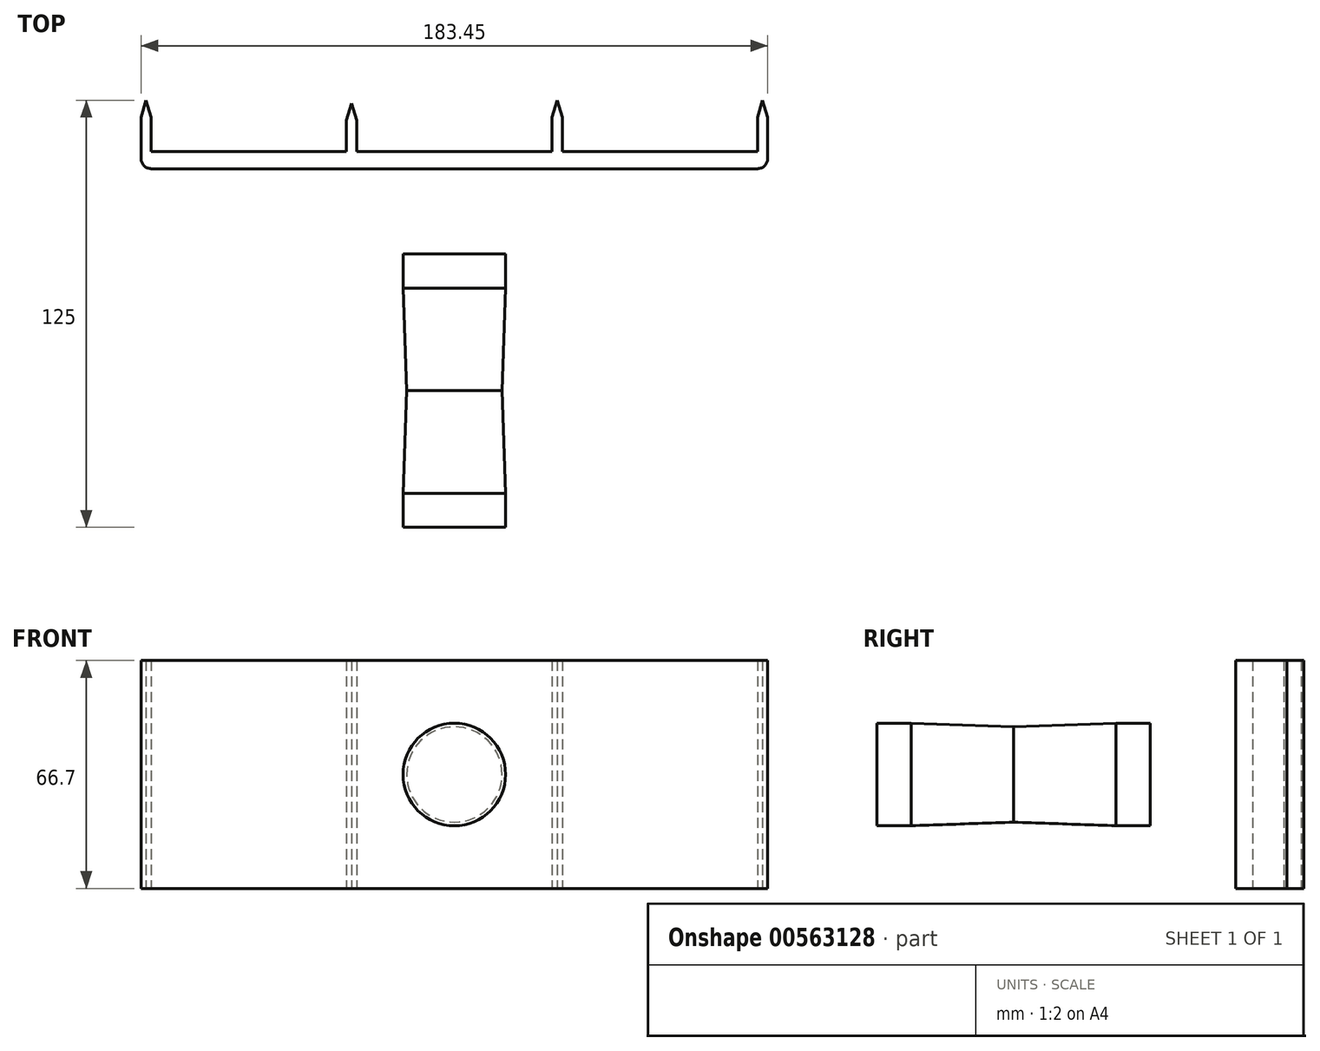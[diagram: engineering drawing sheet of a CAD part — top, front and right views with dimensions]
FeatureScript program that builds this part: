
annotation { "Feature Type Name" : "Feature", "Feature Type Description" : "" }
export const myFeature = defineFeature(function(context is Context, id is Id, definition is map)
    precondition{}
    {
        {
            var Q0;
            Q0=qCreatedBy(makeId("Top.planeOp"),FACE);
            var sketch = newSketch(context, id + "F0", { "sketchPlane" : qUnion([Q0])});
            skLineSegment(sketch, "E0", {"start": v(62.84, 0) * mm, "end": v(62.84, 10) * mm});
            skLineSegment(sketch, "E1", {"start": v(62.84, 0) * mm, "end": v(5.7, 0) * mm});
            skLineSegment(sketch, "E2", {"start": v(5.7, 0) * mm, "end": v(5.7, 10) * mm});
            skLineSegment(sketch, "E3.0", {"start": v(2.7, 0) * mm, "end": v(2.7, 10) * mm});
            skLineSegment(sketch, "E4", {"start": v(2.7, 0) * mm, "end": v(-54.46, 0) * mm});
            skLineSegment(sketch, "E5", {"start": v(-54.46, 0) * mm, "end": v(-54.46, 9.15) * mm});
            skLineSegment(sketch, "E6.0", {"start": v(-57.46, 0) * mm, "end": v(-57.46, 9.15) * mm});
            skLineSegment(sketch, "E7", {"start": v(-57.46, 0) * mm, "end": v(-114.6, 0) * mm});
            skLineSegment(sketch, "E8", {"start": v(-114.6, 0) * mm, "end": v(-114.6, 10) * mm});
            skLineSegment(sketch, "E9.0", {"start": v(-57.46, -5) * mm, "end": v(-114.6, -5) * mm});
            skLineSegment(sketch, "E10.0", {"start": v(2.7, -5) * mm, "end": v(-54.46, -5) * mm});
            skLineSegment(sketch, "E11.0", {"start": v(62.84, -5) * mm, "end": v(5.7, -5) * mm});
            skLineSegment(sketch, "E12", {"start": v(-57.46, -5) * mm, "end": v(-54.46, -5) * mm});
            skLineSegment(sketch, "E13", {"start": v(2.7, -5) * mm, "end": v(5.7, -5) * mm});
            skLineSegment(sketch, "E14.0", {"start": v(65.84, 0) * mm, "end": v(65.84, 10) * mm});
            skLineSegment(sketch, "E15.0", {"start": v(-117.6, 0) * mm, "end": v(-117.6, 10) * mm});
            skLineSegment(sketch, "E16", {"start": v(-117.6, 0) * mm, "end": v(-114.6, 0) * mm});
            skLineSegment(sketch, "E17", {"start": v(-117.6, 0) * mm, "end": v(-117.6, -2) * mm});
            skArc(sketch, "E18", {"start": v(-117.6, -2) * mm, "mid": v(-116.73, -4.12) * mm, "end": v(-114.6, -5) * mm});
            skLineSegment(sketch, "E19", {"start": v(65.84, 0) * mm, "end": v(62.84, 0) * mm});
            skLineSegment(sketch, "E20", {"start": v(65.84, 0) * mm, "end": v(65.84, -2) * mm});
            skArc(sketch, "E21", {"start": v(62.84, -5) * mm, "mid": v(64.96, -4.12) * mm, "end": v(65.84, -2) * mm});
            skLineSegment(sketch, "E22", {"start": v(-114.6, 10) * mm, "end": v(-117.6, 10) * mm});
            skLineSegment(sketch, "E23", {"start": v(-116.1, 10) * mm, "end": v(-116.1, 15) * mm});
            skPoint(sketch, "E23.endSnap0", {"position": v(-116.1, 10) * mm});
            skLineSegment(sketch, "E24", {"start": v(-116.1, 15) * mm, "end": v(-114.6, 10) * mm});
            skLineSegment(sketch, "E25", {"start": v(-116.1, 15) * mm, "end": v(-117.6, 10) * mm});
            skLineSegment(sketch, "E26", {"start": v(-57.46, 9.15) * mm, "end": v(-54.46, 9.15) * mm});
            skLineSegment(sketch, "E27", {"start": v(-55.96, 9.15) * mm, "end": v(-55.96, 14.15) * mm});
            skLineSegment(sketch, "E28", {"start": v(-55.96, 14.15) * mm, "end": v(-54.46, 9.15) * mm});
            skLineSegment(sketch, "E29", {"start": v(-55.96, 14.15) * mm, "end": v(-57.46, 9.15) * mm});
            skLineSegment(sketch, "E30", {"start": v(2.7, 10) * mm, "end": v(5.7, 10) * mm});
            skLineSegment(sketch, "E31", {"start": v(4.2, 10) * mm, "end": v(4.2, 15) * mm});
            skLineSegment(sketch, "E32", {"start": v(4.2, 15) * mm, "end": v(2.7, 10) * mm});
            skLineSegment(sketch, "E33", {"start": v(4.2, 15) * mm, "end": v(5.7, 10) * mm});
            skLineSegment(sketch, "E34", {"start": v(62.84, 10) * mm, "end": v(65.84, 10) * mm});
            skLineSegment(sketch, "E35", {"start": v(64.34, 10) * mm, "end": v(64.34, 15) * mm});
            skLineSegment(sketch, "E36", {"start": v(64.34, 15) * mm, "end": v(62.84, 10) * mm});
            skLineSegment(sketch, "E37", {"start": v(64.34, 15) * mm, "end": v(65.84, 10) * mm});
            skSolve(sketch);
        }
        {
            var Q0;
            Q0 = qSketchRegion(id + "F0", true);
            extrude(context, id + "F1", {"entities" : qUnion([Q0]), "endBound" : BoundingType.SYMMETRIC, "depth" : 66.7 * mm, "offsetDistance" : 25 * mm});
        }
        {
            var Q0;
            Q0=makeQuery(id+"F1.opExtrude","SWEPT_FACE",FACE,{"disambiguationData":[OSD([sQuery(id+"F0.wireOp",EDGE,"E9.0"),sQuery(id+"F0.wireOp",EDGE,"E10.0"),sQuery(id+"F0.wireOp",EDGE,"E11.0"),sQuery(id+"F0.wireOp",EDGE,"E12"),sQuery(id+"F0.wireOp",EDGE,"E13")])]});
            cPlane(context, id + "F2", {"entities" : qUnion([Q0]), "cplaneType" : CPlaneType.OFFSET, "offset" : 25 * mm, "width" : 150 * mm, "height" : 150 * mm});
        }
        {
            var Q0;
            Q0=qCreatedBy(id+"F2.planeOp",FACE);
            var sketch = newSketch(context, id + "F3", { "sketchPlane" : qUnion([Q0])});
            skCircle(sketch, "E38", {"center": v(-25.88, 0) * mm, "radius": 15 * mm});
            skSolve(sketch);
        }
        {
            var Q0;
            Q0 = qSketchRegion(id + "F3", true);
            extrude(context, id + "F4", {"entities" : qUnion([Q0]), "operationType" : NewBodyOperationType.ADD, "depth" : 10 * mm, "offsetDistance" : 25 * mm});
        }
        {
            var Q0;
            Q0=makeQuery(id+"F4.opExtrude","CAP_FACE",FACE,{"disambiguationData":[OSD([sQuery(id+"F3.wireOp",EDGE,"E38")])],"isStart":false});
            extrude(context, id + "F5", {"entities" : qUnion([Q0]), "operationType" : NewBodyOperationType.ADD, "depth" : 30 * mm, "offsetDistance" : 25 * mm, "hasDraft" : true, "draftAngle" : 2 * degree, "draftPullDirection" : true});
        }
        {
            var Q0;
            Q0=makeQuery(id+"F5.opExtrude","CAP_FACE",FACE,{"disambiguationData":[OSD([sQuery(id+"F3.wireOp",EDGE,"E38")])],"isStart":false});
            extrude(context, id + "F6", {"entities" : qUnion([Q0]), "operationType" : NewBodyOperationType.ADD, "depth" : 30 * mm, "offsetDistance" : 25 * mm, "hasDraft" : true, "draftAngle" : 2 * degree});
        }
        {
            var Q0;
            Q0=makeQuery(id+"F6.opExtrude","CAP_FACE",FACE,{"disambiguationData":[OSD([sQuery(id+"F3.wireOp",EDGE,"E38")])],"isStart":false});
            extrude(context, id + "F7", {"entities" : qUnion([Q0]), "operationType" : NewBodyOperationType.ADD, "depth" : 10 * mm, "offsetDistance" : 25 * mm});
        }
    });
